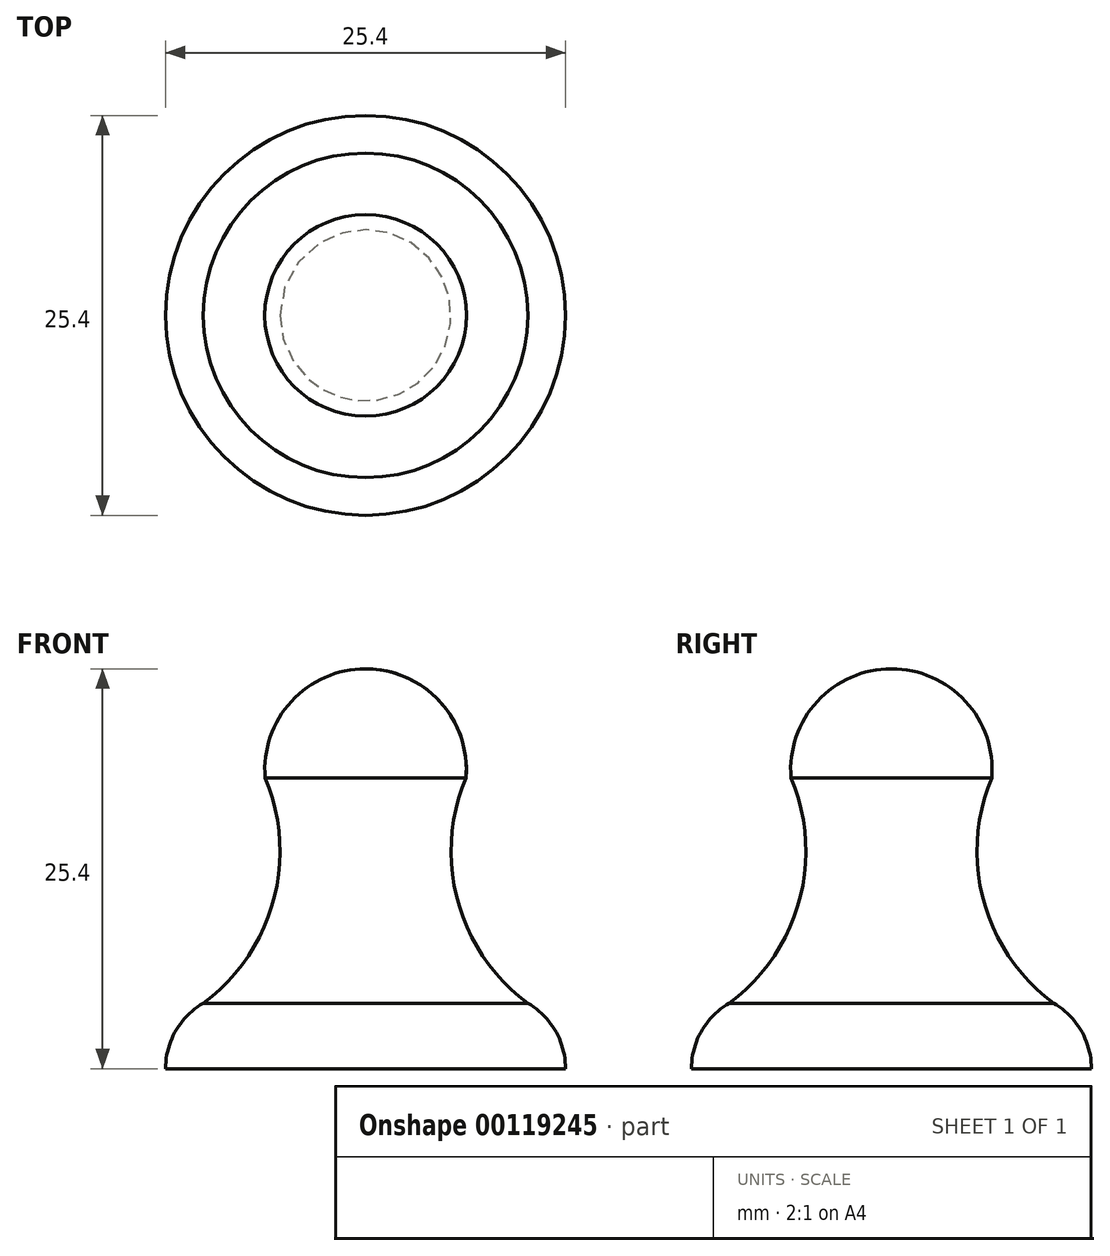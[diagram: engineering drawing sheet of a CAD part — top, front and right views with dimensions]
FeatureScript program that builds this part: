
annotation { "Feature Type Name" : "Feature", "Feature Type Description" : "" }
export const myFeature = defineFeature(function(context is Context, id is Id, definition is map)
    precondition{}
    {
        {
            var Q0;
            Q0=qCreatedBy(makeId("Front.planeOp"),FACE);
            var sketch = newSketch(context, id + "F0", { "sketchPlane" : qUnion([Q0])});
            skLineSegment(sketch, "E0", {"start": v(0, 0) * mm, "end": v(0, 25.4) * mm});
            skLineSegment(sketch, "E1", {"start": v(0, 0) * mm, "end": v(12.7, 0) * mm});
            skArc(sketch, "E2", {"start": v(0, 25.4) * mm, "mid": v(4.7, 23.33) * mm, "end": v(6.38, 18.47) * mm});
            skArc(sketch, "E3", {"start": v(12.7, 0) * mm, "mid": v(12.06, 2.4) * mm, "end": v(10.3, 4.15) * mm});
            skArc(sketch, "E4", {"start": v(6.38, 18.47) * mm, "mid": v(5.86, 10.63) * mm, "end": v(10.3, 4.15) * mm});
            skSolve(sketch);
        }
        {
            var Q0;
            Q0 = qSketchRegion(id + "F0", true);
            var Q1;
            Q1=sQuery(id+"F0.wireOp",EDGE,"E0");
            revolve(context, id + "F1", {"entities" : qUnion([Q0]), "axis" : qUnion([Q1]), "revolveType" : RevolveType.FULL});
        }
    });
